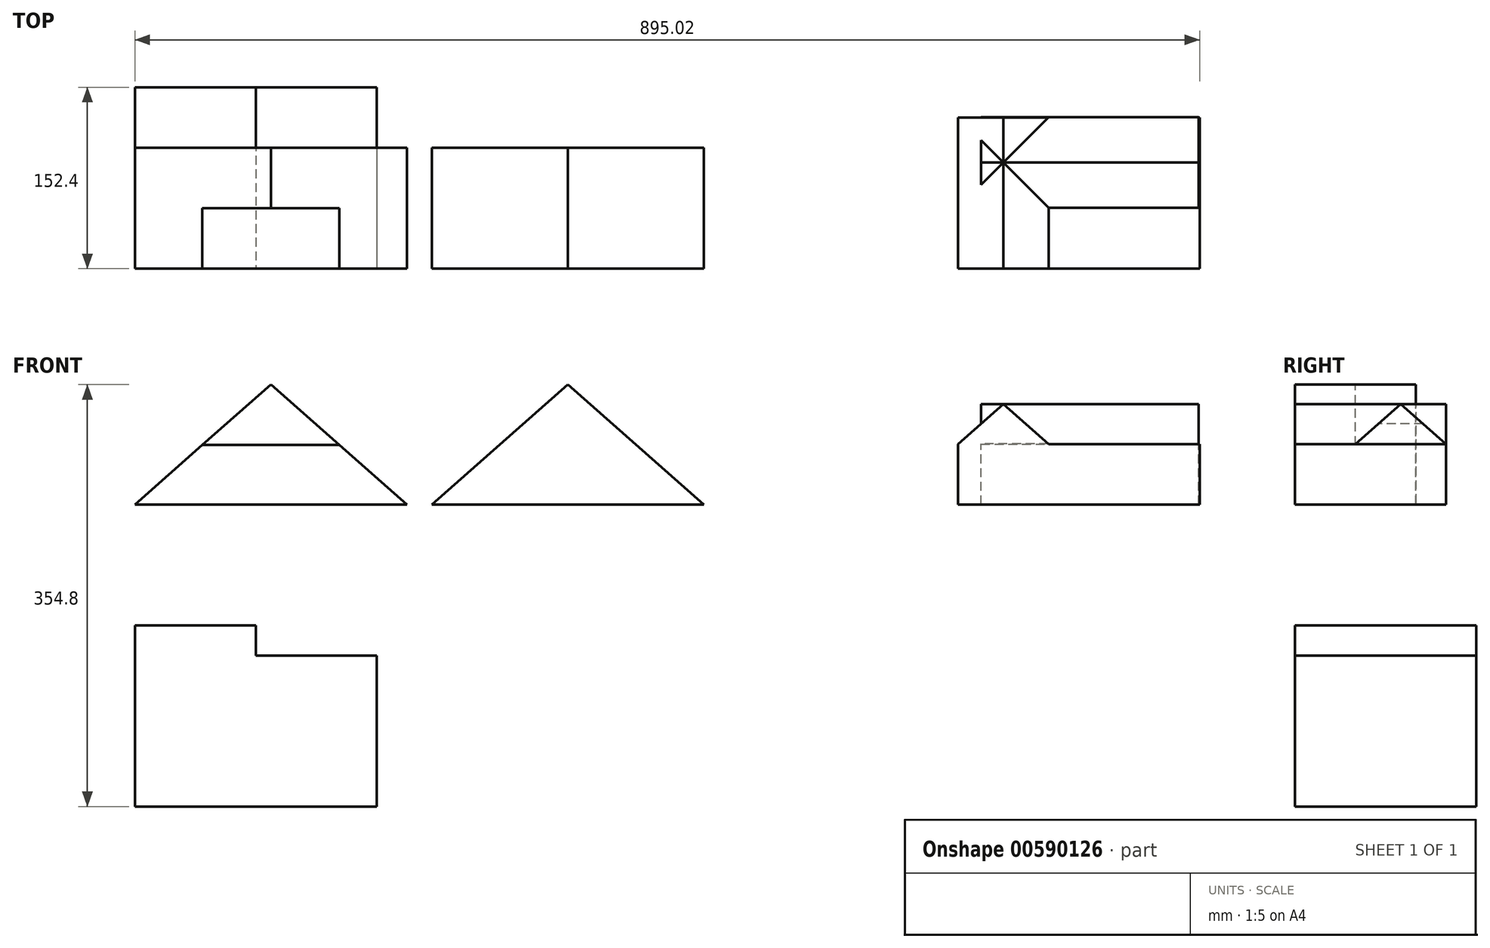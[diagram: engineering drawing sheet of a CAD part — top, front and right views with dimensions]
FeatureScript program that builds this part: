
annotation { "Feature Type Name" : "Feature", "Feature Type Description" : "" }
export const myFeature = defineFeature(function(context is Context, id is Id, definition is map)
    precondition{}
    {
        {
            var Q0;
            Q0=qCreatedBy(makeId("Front.planeOp"),FACE);
            var sketch = newSketch(context, id + "F0", { "sketchPlane" : qUnion([Q0])});
            skLineSegment(sketch, "E0", {"start": v(0, 0) * mm, "end": v(114.3, 100.8) * mm});
            skLineSegment(sketch, "E1", {"start": v(114.3, 100.8) * mm, "end": v(228.6, 0) * mm});
            skLineSegment(sketch, "E2", {"start": v(228.6, 0) * mm, "end": v(0, 0) * mm});
            skSolve(sketch);
        }
        {
            var Q0;
            Q0 = qSketchRegion(id + "F0", true);
            extrude(context, id + "F1", {"entities" : qUnion([Q0]), "oppositeDirection" : true, "depth" : 101.6 * mm, "offsetDistance" : 25.4 * mm});
        }
        {
            var Q0;
            Q0=makeQuery(id+"F1.opExtrude","CAP_FACE",FACE,{"disambiguationData":[OSD([sQuery(id+"F0.wireOp",EDGE,"E0"),sQuery(id+"F0.wireOp",EDGE,"E1"),sQuery(id+"F0.wireOp",EDGE,"E2")])],"isStart":true});
            var sketch = newSketch(context, id + "F2", { "sketchPlane" : qUnion([Q0])});
            skLineSegment(sketch, "E3", {"start": v(56.7, 50) * mm, "end": v(171.9, 50) * mm});
            skSolve(sketch);
        }
        {
            var Q0;
            Q0 = qSketchRegion(id + "F2", true);
            var Q1;
            {var subQ0=sQuery(id+"F2.wireOp",EDGE,"E3");Q1=makeQuery(id+"F2.imprint","IMPRINT",FACE,{"disambiguationData":[TD([[makeQuery(id+"F2.imprint","IMPRINT",EDGE,{"derivedFrom":subQ0}),1.0]])]});}
            extrude(context, id + "F3", {"entities" : qUnion([Q0, Q1]), "operationType" : NewBodyOperationType.ADD, "oppositeDirection" : true, "depth" : 50.8 * mm, "offsetDistance" : 25.4 * mm});
        }
        {
            var Q0;
            {var subQ0=sQuery(id+"F2.wireOp",EDGE,"E3");Q0=makeQuery(id+"F2.imprint","IMPRINT",FACE,{"disambiguationData":[TD([[makeQuery(id+"F2.imprint","IMPRINT",EDGE,{"derivedFrom":subQ0}),1.0]])]});}
            extrude(context, id + "F4", {"entities" : qUnion([Q0]), "operationType" : NewBodyOperationType.REMOVE, "oppositeDirection" : true, "depth" : 50.8 * mm, "offsetDistance" : 25.4 * mm});
        }
        {
            var Q0;
            Q0=qCreatedBy(makeId("Front.planeOp"),FACE);
            var sketch = newSketch(context, id + "F5", { "sketchPlane" : qUnion([Q0])});
            skLineSegment(sketch, "E4", {"start": v(363.84, 100.8) * mm, "end": v(249.54, 0) * mm});
            skLineSegment(sketch, "E5", {"start": v(249.54, 0) * mm, "end": v(478.14, 0) * mm});
            skLineSegment(sketch, "E6", {"start": v(478.14, 0) * mm, "end": v(363.84, 100.8) * mm});
            skLineSegment(sketch, "E7", {"start": v(306.69, 50.4) * mm, "end": v(420.99, 50.4) * mm});
            skPoint(sketch, "E7.endSnap0", {"position": v(420.99, 50.4) * mm});
            skSolve(sketch);
        }
        {
            var Q0;
            Q0 = qSketchRegion(id + "F5", true);
            extrude(context, id + "F6", {"entities" : qUnion([Q0]), "oppositeDirection" : true, "depth" : 101.6 * mm, "offsetDistance" : 25.4 * mm});
        }
        {
            var Q0;
            Q0=qCreatedBy(makeId("Right.planeOp"),FACE);
            cPlane(context, id + "F7", {"entities" : qUnion([Q0]), "cplaneType" : CPlaneType.OFFSET, "offset" : 894.08 * mm, "width" : 152.4 * mm, "height" : 152.4 * mm});
        }
        {
            var Q0;
            Q0=qCreatedBy(id+"F7.planeOp",FACE);
            var sketch = newSketch(context, id + "F8", { "sketchPlane" : qUnion([Q0])});
            skLineSegment(sketch, "E8", {"start": v(50.8, 100.8) * mm, "end": v(0, 24.6) * mm});
            skLineSegment(sketch, "E9", {"start": v(0, 24.6) * mm, "end": v(0, 100.8) * mm});
            skLineSegment(sketch, "E10", {"start": v(0, 100.8) * mm, "end": v(50.8, 100.8) * mm});
            skSolve(sketch);
        }
        {
            var Q0;
            Q0=makeQuery(id+"F8.imprint","IMPRINT",FACE,{"disambiguationData":[TD([[makeQuery(id+"F8.imprint","IMPRINT",EDGE,{"derivedFrom":sQuery(id+"F8.wireOp",EDGE,"E8")}),-1.0]])]});
            extrude(context, id + "F9", {"entities" : qUnion([Q0]), "operationType" : NewBodyOperationType.REMOVE, "oppositeDirection" : true, "depth" : 279.4 * mm, "offsetDistance" : 25.4 * mm});
        }
        {
            var Q0;
            Q0=qCreatedBy(makeId("Front.planeOp"),FACE);
            var sketch = newSketch(context, id + "F10", { "sketchPlane" : qUnion([Q0])});
            skLineSegment(sketch, "E11", {"start": v(691.82, 50.8) * mm, "end": v(691.82, 0) * mm});
            skLineSegment(sketch, "E12", {"start": v(691.82, 0) * mm, "end": v(768.02, 0) * mm});
            skLineSegment(sketch, "E13", {"start": v(768.02, 0) * mm, "end": v(768.02, 50.8) * mm});
            skLineSegment(sketch, "E14", {"start": v(691.82, 50.8) * mm, "end": v(729.92, 84.4) * mm});
            skLineSegment(sketch, "E15", {"start": v(729.92, 84.4) * mm, "end": v(768.02, 50.8) * mm});
            skSolve(sketch);
        }
        {
            var Q0;
            Q0 = qSketchRegion(id + "F10", true);
            extrude(context, id + "F11", {"entities" : qUnion([Q0]), "oppositeDirection" : true, "depth" : 127 * mm, "offsetDistance" : 25.4 * mm});
        }
        {
            var Q0;
            Q0=qCreatedBy(makeId("Front.planeOp"),FACE);
            var sketch = newSketch(context, id + "F12", { "sketchPlane" : qUnion([Q0])});
            skLineSegment(sketch, "E16", {"start": v(768.02, 50.8) * mm, "end": v(895.02, 50.8) * mm});
            skLineSegment(sketch, "E17", {"start": v(895.02, 50.8) * mm, "end": v(895.02, 0) * mm});
            skLineSegment(sketch, "E18", {"start": v(895.02, 0) * mm, "end": v(768.02, 0) * mm});
            skLineSegment(sketch, "E19", {"start": v(895.02, 50.8) * mm, "end": v(895.02, 76.2) * mm});
            skLineSegment(sketch, "E20", {"start": v(895.02, 76.2) * mm, "end": v(737.75, 76.2) * mm});
            skLineSegment(sketch, "E21", {"start": v(768.02, 50.8) * mm, "end": v(768.02, 0) * mm});
            skSolve(sketch);
        }
        {
            var Q0;
            Q0 = qSketchRegion(id + "F12", true);
            extrude(context, id + "F13", {"entities" : qUnion([Q0]), "operationType" : NewBodyOperationType.ADD, "oppositeDirection" : true, "depth" : 127 * mm, "offsetDistance" : 25.4 * mm});
        }
        {
            var Q0;
            Q0=qCreatedBy(id+"F7.planeOp",FACE);
            var sketch = newSketch(context, id + "F14", { "sketchPlane" : qUnion([Q0])});
            skLineSegment(sketch, "E22", {"start": v(89.12, 84.4) * mm, "end": v(51.02, 50.8) * mm});
            skLineSegment(sketch, "E23", {"start": v(51.02, 50.8) * mm, "end": v(127.22, 50.8) * mm});
            skLineSegment(sketch, "E24", {"start": v(127.22, 50.8) * mm, "end": v(89.12, 84.4) * mm});
            skLineSegment(sketch, "E25", {"start": v(51.02, 50.8) * mm, "end": v(51.02, 0) * mm});
            skLineSegment(sketch, "E26", {"start": v(51.02, 0) * mm, "end": v(127.22, 0) * mm});
            skLineSegment(sketch, "E27", {"start": v(127.22, 0) * mm, "end": v(127.22, 50.8) * mm});
            skSolve(sketch);
        }
        {
            var Q0;
            Q0 = qSketchRegion(id + "F14", true);
            extrude(context, id + "F15", {"entities" : qUnion([Q0]), "operationType" : NewBodyOperationType.ADD, "oppositeDirection" : true, "depth" : 182.88 * mm, "offsetDistance" : 25.4 * mm});
        }
        {
            var Q0;
            Q0=qCreatedBy(makeId("Front.planeOp"),FACE);
            var sketch = newSketch(context, id + "F16", { "sketchPlane" : qUnion([Q0])});
            skLineSegment(sketch, "E28", {"start": v(0, -101.6) * mm, "end": v(0, -254) * mm});
            skLineSegment(sketch, "E29", {"start": v(0, -254) * mm, "end": v(203.2, -254) * mm});
            skLineSegment(sketch, "E30", {"start": v(203.2, -254) * mm, "end": v(203.2, -127) * mm});
            skLineSegment(sketch, "E31", {"start": v(203.2, -127) * mm, "end": v(101.6, -127) * mm});
            skLineSegment(sketch, "E32", {"start": v(101.6, -127) * mm, "end": v(101.6, -101.6) * mm});
            skLineSegment(sketch, "E33", {"start": v(101.6, -101.6) * mm, "end": v(0, -101.6) * mm});
            skSolve(sketch);
        }
        {
            var Q0;
            Q0 = qSketchRegion(id + "F16", true);
            extrude(context, id + "F17", {"entities" : qUnion([Q0]), "oppositeDirection" : true, "depth" : 152.4 * mm, "offsetDistance" : 25.4 * mm});
        }
    });
